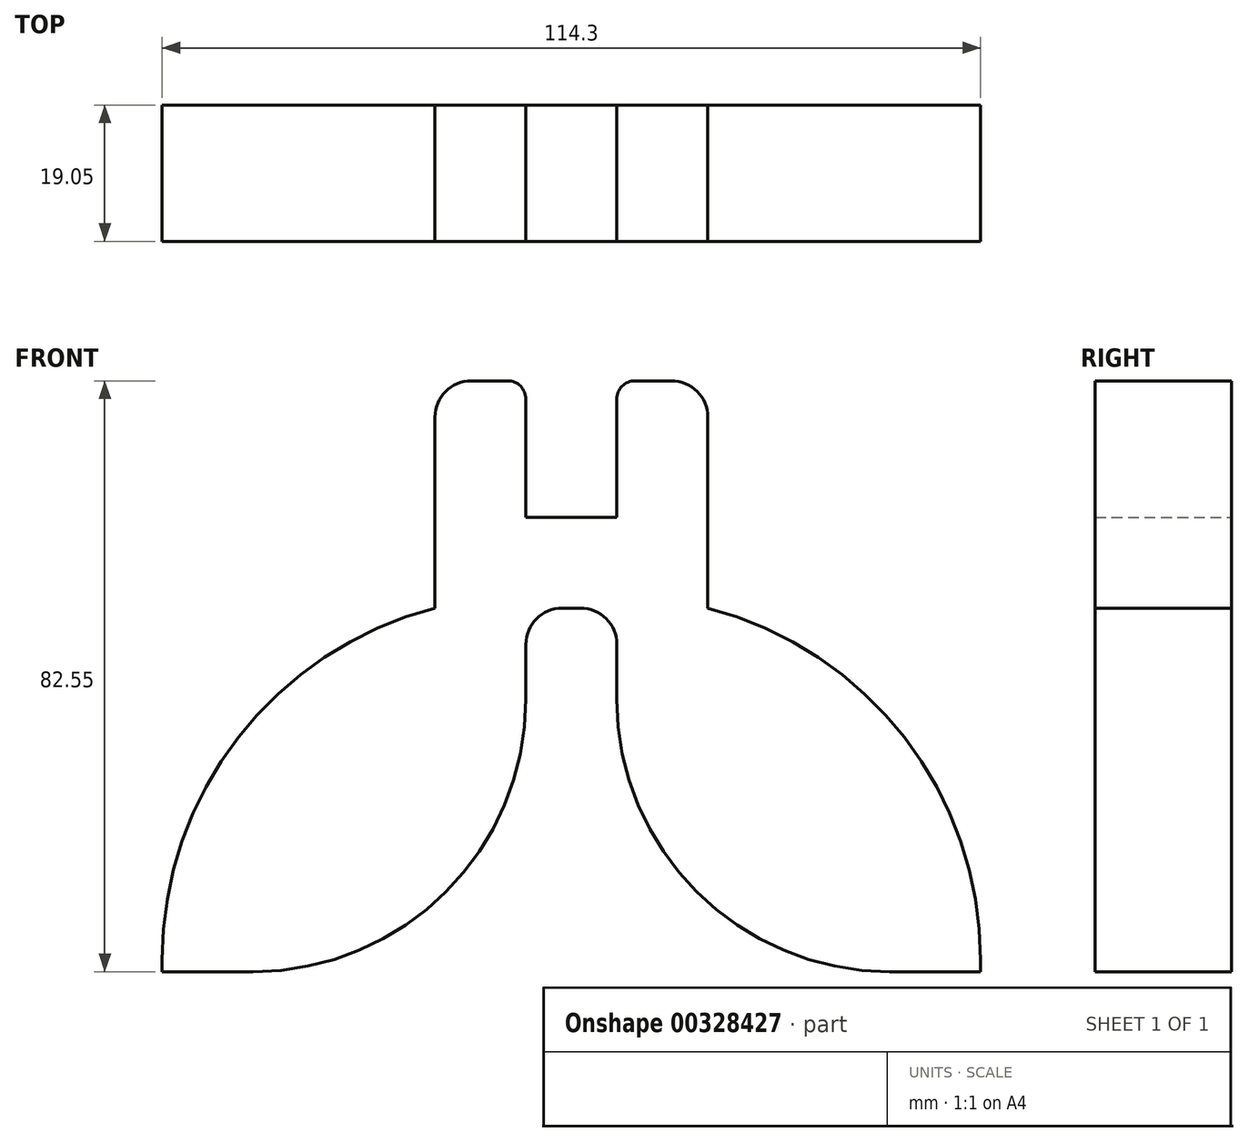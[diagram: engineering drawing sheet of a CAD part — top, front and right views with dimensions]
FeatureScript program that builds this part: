
annotation { "Feature Type Name" : "Feature", "Feature Type Description" : "" }
export const myFeature = defineFeature(function(context is Context, id is Id, definition is map)
    precondition{}
    {
        {
            var Q0;
            Q0=qCreatedBy(makeId("Front.planeOp"),FACE);
            var sketch = newSketch(context, id + "F0", { "sketchPlane" : qUnion([Q0])});
            skLineSegment(sketch, "E0.bottom", {"start": v(0, 0) * mm, "end": v(-6.35, 0) * mm});
            skLineSegment(sketch, "E0.top", {"start": v(0, 12.7) * mm, "end": v(-6.35, 12.7) * mm});
            skLineSegment(sketch, "E0.left", {"start": v(0, 0) * mm, "end": v(0, 12.7) * mm});
            skLineSegment(sketch, "E0.right", {"start": v(-6.35, 0) * mm, "end": v(-6.35, 12.7) * mm});
            skLineSegment(sketch, "E1.bottom", {"start": v(0, 0) * mm, "end": v(6.35, 0) * mm});
            skLineSegment(sketch, "E1.top", {"start": v(0, 12.7) * mm, "end": v(6.35, 12.7) * mm});
            skLineSegment(sketch, "E1.right", {"start": v(6.35, 0) * mm, "end": v(6.35, 12.7) * mm});
            skLineSegment(sketch, "E2.bottom", {"start": v(6.35, 0) * mm, "end": v(19.05, 0) * mm});
            skLineSegment(sketch, "E2.top", {"start": v(6.35, 31.75) * mm, "end": v(19.05, 31.75) * mm});
            skLineSegment(sketch, "E2.left", {"start": v(6.35, 0) * mm, "end": v(6.35, 31.75) * mm});
            skLineSegment(sketch, "E2.right", {"start": v(19.05, 0) * mm, "end": v(19.05, 31.75) * mm});
            skLineSegment(sketch, "E3.bottom", {"start": v(-6.35, 0) * mm, "end": v(-19.05, 0) * mm});
            skLineSegment(sketch, "E3.top", {"start": v(-6.35, 31.75) * mm, "end": v(-19.05, 31.75) * mm});
            skLineSegment(sketch, "E3.left", {"start": v(-6.35, 0) * mm, "end": v(-6.35, 31.75) * mm});
            skLineSegment(sketch, "E3.right", {"start": v(-19.05, 0) * mm, "end": v(-19.05, 31.75) * mm});
            skLineSegment(sketch, "E4.bottom", {"start": v(-6.35, 0) * mm, "end": v(-57.15, 0) * mm});
            skLineSegment(sketch, "E4.top", {"start": v(-6.35, -50.8) * mm, "end": v(-57.15, -50.8) * mm});
            skLineSegment(sketch, "E4.left", {"start": v(-6.35, 0) * mm, "end": v(-6.35, -50.8) * mm});
            skLineSegment(sketch, "E4.right", {"start": v(-57.15, 0) * mm, "end": v(-57.15, -50.8) * mm});
            skLineSegment(sketch, "E5.bottom", {"start": v(6.35, 0) * mm, "end": v(57.15, 0) * mm});
            skLineSegment(sketch, "E5.right", {"start": v(57.15, 0) * mm, "end": v(57.15, -50.8) * mm});
            skLineSegment(sketch, "E6", {"start": v(6.35, 0) * mm, "end": v(6.35, -50.8) * mm});
            skLineSegment(sketch, "E7", {"start": v(6.35, -50.8) * mm, "end": v(57.15, -50.8) * mm});
            skSolve(sketch);
        }
        {
            var Q0;
            Q0=makeQuery(id+"F0.imprint","IMPRINT",FACE,{"disambiguationData":[TD([[makeQuery(id+"F0.imprint","IMPRINT",EDGE,{"derivedFrom":sQuery(id+"F0.wireOp",EDGE,"E4.top")}),-1.0]])]});
            var Q1;
            {var subQ3=sQuery(id+"F0.wireOp",EDGE,"E3.top");Q1=makeQuery(id+"F0.imprint","IMPRINT",FACE,{"disambiguationData":[TD([[makeQuery(id+"F0.imprint","IMPRINT",EDGE,{"derivedFrom":subQ3}),1.0]])]});}
            var Q2;
            {var subQ0=sQuery(id+"F0.wireOp",EDGE,"E0.bottom");Q2=makeQuery(id+"F0.imprint","IMPRINT",FACE,{"disambiguationData":[TD([[makeQuery(id+"F0.imprint","IMPRINT",EDGE,{"derivedFrom":subQ0}),-1.0]])]});}
            var Q3;
            {var subQ0=sQuery(id+"F0.wireOp",EDGE,"E1.bottom");Q3=makeQuery(id+"F0.imprint","IMPRINT",FACE,{"disambiguationData":[TD([[makeQuery(id+"F0.imprint","IMPRINT",EDGE,{"derivedFrom":subQ0}),1.0]])]});}
            var Q4;
            {var subQ3=sQuery(id+"F0.wireOp",EDGE,"E2.top");Q4=makeQuery(id+"F0.imprint","IMPRINT",FACE,{"disambiguationData":[TD([[makeQuery(id+"F0.imprint","IMPRINT",EDGE,{"derivedFrom":subQ3}),-1.0]])]});}
            var Q5;
            {var subQ1=sQuery(id+"F0.wireOp",EDGE,"E5.right");Q5=makeQuery(id+"F0.imprint","IMPRINT",FACE,{"disambiguationData":[TD([[makeQuery(id+"F0.imprint","IMPRINT",EDGE,{"derivedFrom":subQ1}),-1.0]])]});}
            extrude(context, id + "F1", {"entities" : qUnion([Q0, Q1, Q2, Q3, Q4, Q5]), "depth" : 19.05 * mm});
        }
        {
            var Q0;
            Q0=makeQuery(id+"F1.opExtrude","SWEPT_EDGE",EDGE,{"disambiguationData":[OSD([sQuery(id+"F0.wireOp",EDGE,"E2.top"),sQuery(id+"F0.wireOp",EDGE,"E2.left")])]});
            var Q1;
            Q1=makeQuery(id+"F1.opExtrude","SWEPT_EDGE",EDGE,{"disambiguationData":[OSD([sQuery(id+"F0.wireOp",EDGE,"E3.top"),sQuery(id+"F0.wireOp",EDGE,"E3.left")])]});
            fillet(context, id + "F2", {"entities" : qUnion([Q0, Q1]), "radius" : 2.54 * mm, "tangentPropagation" : true, "allowEdgeOverflow" : false});
        }
        {
            var Q0;
            Q0=makeQuery(id+"F1.opExtrude","SWEPT_EDGE",EDGE,{"disambiguationData":[OSD([sQuery(id+"F0.wireOp",EDGE,"E6"),sQuery(id+"F0.wireOp",EDGE,"E7")])]});
            var Q1;
            Q1=makeQuery(id+"F1.opExtrude","SWEPT_EDGE",EDGE,{"disambiguationData":[OSD([sQuery(id+"F0.wireOp",EDGE,"E4.top"),sQuery(id+"F0.wireOp",EDGE,"E4.left")])]});
            fillet(context, id + "F3", {"entities" : qUnion([Q0, Q1]), "radius" : 38.1 * mm, "tangentPropagation" : true, "allowEdgeOverflow" : false});
        }
        {
            var Q0;
            Q0=makeQuery(id+"F1.opExtrude","SWEPT_EDGE",EDGE,{"disambiguationData":[OSD([sQuery(id+"F0.wireOp",EDGE,"E4.bottom"),sQuery(id+"F0.wireOp",EDGE,"E4.right")])]});
            var Q1;
            Q1=makeQuery(id+"F1.opExtrude","SWEPT_EDGE",EDGE,{"disambiguationData":[OSD([sQuery(id+"F0.wireOp",EDGE,"E5.bottom"),sQuery(id+"F0.wireOp",EDGE,"E5.right")])]});
            fillet(context, id + "F4", {"entities" : qUnion([Q0, Q1]), "radius" : 50.8 * mm, "tangentPropagation" : true, "allowEdgeOverflow" : false});
        }
        {
            var Q0;
            Q0=makeQuery(id+"F1.opExtrude","SWEPT_EDGE",EDGE,{"disambiguationData":[OSD([sQuery(id+"F0.wireOp",EDGE,"E3.top"),sQuery(id+"F0.wireOp",EDGE,"E3.right")])]});
            var Q1;
            Q1=makeQuery(id+"F1.opExtrude","SWEPT_EDGE",EDGE,{"disambiguationData":[OSD([sQuery(id+"F0.wireOp",EDGE,"E2.top"),sQuery(id+"F0.wireOp",EDGE,"E2.right")])]});
            fillet(context, id + "F5", {"entities" : qUnion([Q0, Q1]), "radius" : 5.08 * mm, "tangentPropagation" : true, "allowEdgeOverflow" : false});
        }
        {
            var Q0;
            Q0=makeQuery(id+"F1.opExtrude","SWEPT_EDGE",EDGE,{"disambiguationData":[OSD([sQuery(id+"F0.wireOp",EDGE,"E1.bottom"),sQuery(id+"F0.wireOp",EDGE,"E2.left"),sQuery(id+"F0.wireOp",EDGE,"E5.bottom"),sQuery(id+"F0.wireOp",EDGE,"E6")])]});
            var Q1;
            Q1=makeQuery(id+"F1.opExtrude","SWEPT_EDGE",EDGE,{"disambiguationData":[OSD([sQuery(id+"F0.wireOp",EDGE,"E0.bottom"),sQuery(id+"F0.wireOp",EDGE,"E3.left"),sQuery(id+"F0.wireOp",EDGE,"E4.bottom"),sQuery(id+"F0.wireOp",EDGE,"E4.left")])]});
            fillet(context, id + "F6", {"entities" : qUnion([Q0, Q1]), "radius" : 5.08 * mm, "tangentPropagation" : true, "allowEdgeOverflow" : false});
        }
    });
